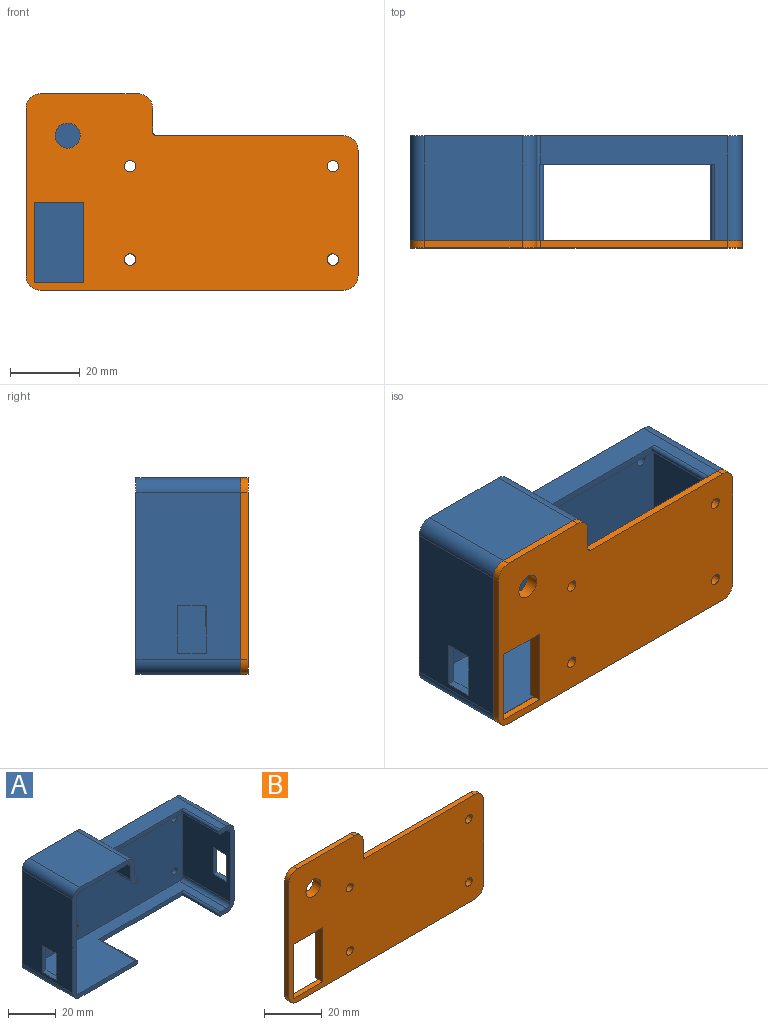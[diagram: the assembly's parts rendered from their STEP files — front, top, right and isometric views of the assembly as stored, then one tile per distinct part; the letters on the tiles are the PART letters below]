
ASSEMBLY  parts=2 mates=1
PART A: 45 faces, bbox 95.4x30.1x56.4 mm
  f0: plane 48x30.1mm, normal (-1,0,0), area 1332.5mm2, adj f4,f16,f24,f28,f41,f42,f43,f44
  f1: plane 50x28mm, normal (1,0,0), area 1287.7mm2, adj f4,f8,f17,f20,f41,f42,f43,f44
  f2: plane 36x30.1mm, normal (1,0,0), area 974.8mm2, adj f7,f16,f25,f26,f37,f38,f39,f40
  f3: plane 36x28mm, normal (-1,0,0), area 899.2mm2, adj f7,f8,f22,f23,f37,f38,f39,f40
  f4: plane 56.4x38.4mm, normal (0,-1,0), area 297.1mm2, adj f0,f1,f9,f10,f15,f17,f18,f19
  f5: plane 53.8x30.1mm, normal (0,0,1), area 517.2mm2, adj f7,f16,f26,f30,f31,f33
  f6: plane 53.8x28mm, normal (0,0,-1), area 404.2mm2, adj f7,f8,f22,f30,f32,f33
  f7: plane 44.4x9mm, normal (0,-1,0), area 120.7mm2, adj f2,f3,f5,f6,f9,f17,f22,f23
  f8: plane 91x52mm, normal (0,-1,0), area 3988.6mm2, adj f1,f3,f6,f11,f12,f13,f14,f17
  f9: plane 87x30.1mm, normal (0,0,-1), area 1514.3mm2, adj f4,f7,f16,f24,f25,f29,f35,f36
  f10: plane 30.1x6.8mm, normal (1,0,0), area 204.7mm2, adj f4,f16,f27,f31
  f11: cylinder r=1.65mm len=3.3mm, axis (0,-1,0), area 21.8mm2, adj f8,f16
  f12: cylinder r=1.65mm len=3.3mm, axis (0,-1,0), area 21.8mm2, adj f8,f16
  f13: cylinder r=1.65mm len=3.3mm, axis (0,-1,0), area 21.8mm2, adj f8,f16
  f14: cylinder r=1.65mm len=3.3mm, axis (0,-1,0), area 21.8mm2, adj f8,f16
  f15: plane 30.1x28mm, normal (0,0,1), area 842.8mm2, adj f4,f16,f27,f28
  f16: plane 95.4x56.4mm, normal (0,1,0), area 4619.6mm2, adj f0,f2,f5,f9,f10,f11,f12,f13
  f17: plane 89x28mm, normal (0,0,1), area 1387.6mm2, adj f1,f4,f7,f8,f23,f29,f35,f36
  f18: plane 28x28mm, normal (0,0,-1), area 784mm2, adj f4,f8,f20,f21
  f19: plane 28x6.8mm, normal (-1,0,0), area 190.4mm2, adj f4,f8,f21,f32
  f20: cylinder r=2mm len=28mm, axis (0,1,0), area 88mm2, adj f1,f4,f8,f18
  f21: cylinder r=2mm len=28mm, axis (0,1,0), area 88mm2, adj f4,f8,f18,f19
  f22: cylinder r=2mm len=28mm, axis (0,-1,0), area 88mm2, adj f3,f6,f7,f8
  f23: cylinder r=2mm len=28mm, axis (0,1,0), area 88mm2, adj f3,f7,f8,f17
  f24: cylinder r=4.2mm len=30.1mm, axis (0,1,0), area 198.6mm2, adj f0,f4,f9,f16
  f25: cylinder r=4.2mm len=30.1mm, axis (0,-1,0), area 198.6mm2, adj f2,f7,f9,f16
  f26: cylinder r=4.2mm len=30.1mm, axis (0,1,0), area 198.6mm2, adj f2,f5,f7,f16
  f27: cylinder r=4.2mm len=30.1mm, axis (0,1,0), area 198.6mm2, adj f4,f10,f15,f16
  f28: cylinder r=4.2mm len=30.1mm, axis (0,-1,0), area 198.6mm2, adj f0,f4,f15,f16
  f29: plane 50.2x2.2mm, normal (0,-1,0), area 106.6mm2, adj f9,f17,f35,f36
  f30: plane 50.25x2.2mm, normal (0,-1,0), area 106.6mm2, adj f5,f6,f31,f32,f33,f34
  f31: cylinder r=1mm len=30.1mm, axis (0,-1,0), area 46.2mm2, adj f4,f5,f10,f16,f30,f34
  f32: cylinder r=3.2mm len=28mm, axis (0,-1,0), area 137.4mm2, adj f4,f6,f8,f19,f30,f34
  f33: cylinder r=1.1mm len=22mm, axis (0,1,0), area 76mm2, adj f5,f6,f7,f30
  f34: cylinder r=1.1mm len=22mm, axis (0,-1,0), area 76mm2, adj f4,f30,f31,f32
  f35: cylinder r=1.1mm len=22mm, axis (0,1,0), area 76mm2, adj f7,f9,f17,f29
  f36: cylinder r=1.1mm len=22mm, axis (0,-1,0), area 76mm2, adj f4,f9,f17,f29
  f37: plane 8x2.2mm, normal (0,0,-1), area 17.6mm2, adj f2,f3,f38,f40
  f38: plane 13.6x2.2mm, normal (0,1,0), area 29.9mm2, adj f2,f3,f37,f39
  f39: plane 8x2.2mm, normal (0,0,1), area 17.6mm2, adj f2,f3,f38,f40
  f40: plane 13.6x2.2mm, normal (0,-1,0), area 29.9mm2, adj f2,f3,f37,f39
  f41: plane 8.2x2.2mm, normal (0,0,-1), area 18mm2, adj f0,f1,f42,f44
  f42: plane 13.7x2.2mm, normal (0,-1,0), area 30.1mm2, adj f0,f1,f41,f43
  f43: plane 8.2x2.2mm, normal (0,0,1), area 18mm2, adj f0,f1,f42,f44
  f44: plane 13.7x2.2mm, normal (0,1,0), area 30.1mm2, adj f0,f1,f41,f43
PART B: 43 faces, bbox 95.4x3.6x56.4 mm
  f0: plane 19.8x1.5mm, normal (0,0,-1), area 29.7mm2, adj f4,f20,f31,f37
  f1: plane 39.8x6.7mm, normal (0,1,0), area 246.1mm2, adj f2,f3,f8,f10,f11,f33,f35,f36
  f2: plane 2.7x1.5mm, normal (0,0,1), area 4.1mm2, adj f1,f20,f35,f41
  f3: plane 2.7x1.5mm, normal (0,0,-1), area 4.1mm2, adj f1,f20,f36,f40
  f4: plane 51.8x36.1mm, normal (0,1,0), area 1430.7mm2, adj f0,f6,f7,f9,f12,f13,f27,f30
  f5: plane 95.4x56.4mm, normal (0,-1,0), area 4250mm2, adj f9,f10,f11,f13,f14,f15,f16,f17
  f6: plane 27.8x1.5mm, normal (0,0,1), area 41.7mm2, adj f4,f20,f39,f42
  f7: plane 26.8x1.5mm, normal (-1,0,0), area 40.2mm2, adj f4,f20,f30,f39
  f8: plane 35.8x1.5mm, normal (1,0,0), area 53.7mm2, adj f1,f20,f40,f41
  f9: cylinder r=1.65mm len=3.6mm, axis (0,-1,0), area 37.3mm2, adj f4,f5
  f10: cylinder r=1.65mm len=3.6mm, axis (0,-1,0), area 37.3mm2, adj f1,f5
  f11: cylinder r=1.65mm len=3.6mm, axis (0,-1,0), area 37.3mm2, adj f1,f5
  f12: plane 6.7x1.5mm, normal (1,0,0), area 10.1mm2, adj f4,f20,f27,f42
  f13: cylinder r=1.65mm len=3.6mm, axis (0,-1,0), area 37.3mm2, adj f4,f5
  f14: plane 48x2.1mm, normal (-1,0,0), area 100.8mm2, adj f5,f20,f21,f25
  f15: plane 87x2.1mm, normal (0,0,-1), area 182.7mm2, adj f5,f20,f21,f22
  f16: plane 36x2.1mm, normal (1,0,0), area 75.6mm2, adj f5,f20,f22,f23
  f17: plane 53.8x2.1mm, normal (0,0,1), area 113mm2, adj f5,f20,f23,f26
  f18: plane 6.8x2.1mm, normal (1,0,0), area 14.3mm2, adj f5,f20,f24,f26
  f19: plane 28x2.1mm, normal (0,0,1), area 58.8mm2, adj f5,f20,f24,f25
  f20: plane 95.4x56.4mm, normal (0,1,0), area 2573.2mm2, adj f0,f2,f3,f6,f7,f8,f12,f14
  f21: cylinder r=4.2mm len=4.2mm, axis (0,-1,0), area 13.9mm2, adj f5,f14,f15,f20
  f22: cylinder r=4.2mm len=4.2mm, axis (0,1,0), area 13.9mm2, adj f5,f15,f16,f20
  f23: cylinder r=4.2mm len=4.2mm, axis (0,-1,0), area 13.9mm2, adj f5,f16,f17,f20
  f24: cylinder r=4.2mm len=4.2mm, axis (0,-1,0), area 13.9mm2, adj f5,f18,f19,f20
  f25: cylinder r=4.2mm len=4.2mm, axis (0,1,0), area 13.9mm2, adj f5,f14,f19,f20
  f26: cylinder r=1mm len=2.1mm, axis (0,1,0), area 3.3mm2, adj f5,f17,f18,f20
  f27: cylinder r=3.3mm len=3.24mm, axis (0,1,0), area 6.8mm2, adj f4,f12,f20,f38
  f28: plane 23x2.1mm, normal (1,0,0), area 48.3mm2, adj f5,f20,f29,f30
  f29: plane 14.3x2.1mm, normal (0,0,1), area 30mm2, adj f5,f20,f28,f31
  f30: plane 14.3x3.6mm, normal (0,0,-1), area 51.5mm2, adj f4,f5,f7,f28,f31
  f31: plane 23x3.6mm, normal (-1,0,0), area 82.8mm2, adj f0,f4,f5,f29,f30
  f32: cylinder r=3.6mm len=7.2mm, axis (0,-1,0), area 81.4mm2, adj f4,f5
  f33: plane 35.8x1.5mm, normal (-1,0,0), area 53.7mm2, adj f1,f20,f35,f36
  f34: plane 35.9x1.5mm, normal (1,0,0), area 53.8mm2, adj f4,f20,f37,f38
  f35: cylinder r=2mm len=2mm, axis (0,1,0), area 4.7mm2, adj f1,f2,f20,f33
  f36: cylinder r=2mm len=2mm, axis (0,1,0), area 4.7mm2, adj f1,f3,f20,f33
  f37: cylinder r=2mm len=2mm, axis (0,-1,0), area 4.7mm2, adj f0,f4,f20,f34
  f38: cylinder r=2mm len=1.96mm, axis (0,1,0), area 4.1mm2, adj f4,f20,f27,f34
  f39: cylinder r=2mm len=2mm, axis (0,-1,0), area 4.7mm2, adj f4,f6,f7,f20
  f40: cylinder r=2mm len=2mm, axis (0,-1,0), area 4.7mm2, adj f1,f3,f8,f20
  f41: cylinder r=2mm len=2mm, axis (0,-1,0), area 4.7mm2, adj f1,f2,f8,f20
  f42: cylinder r=2mm len=2mm, axis (0,-1,0), area 4.7mm2, adj f4,f6,f12,f20
PLACE A t=(0,32.8,0)mm
PLACE B t=(0,4.8,0)mm
MATE fastened B.f20 <-> A.f4  axis (0,1,0) through (-38.31,4.8,-42.2)mm
